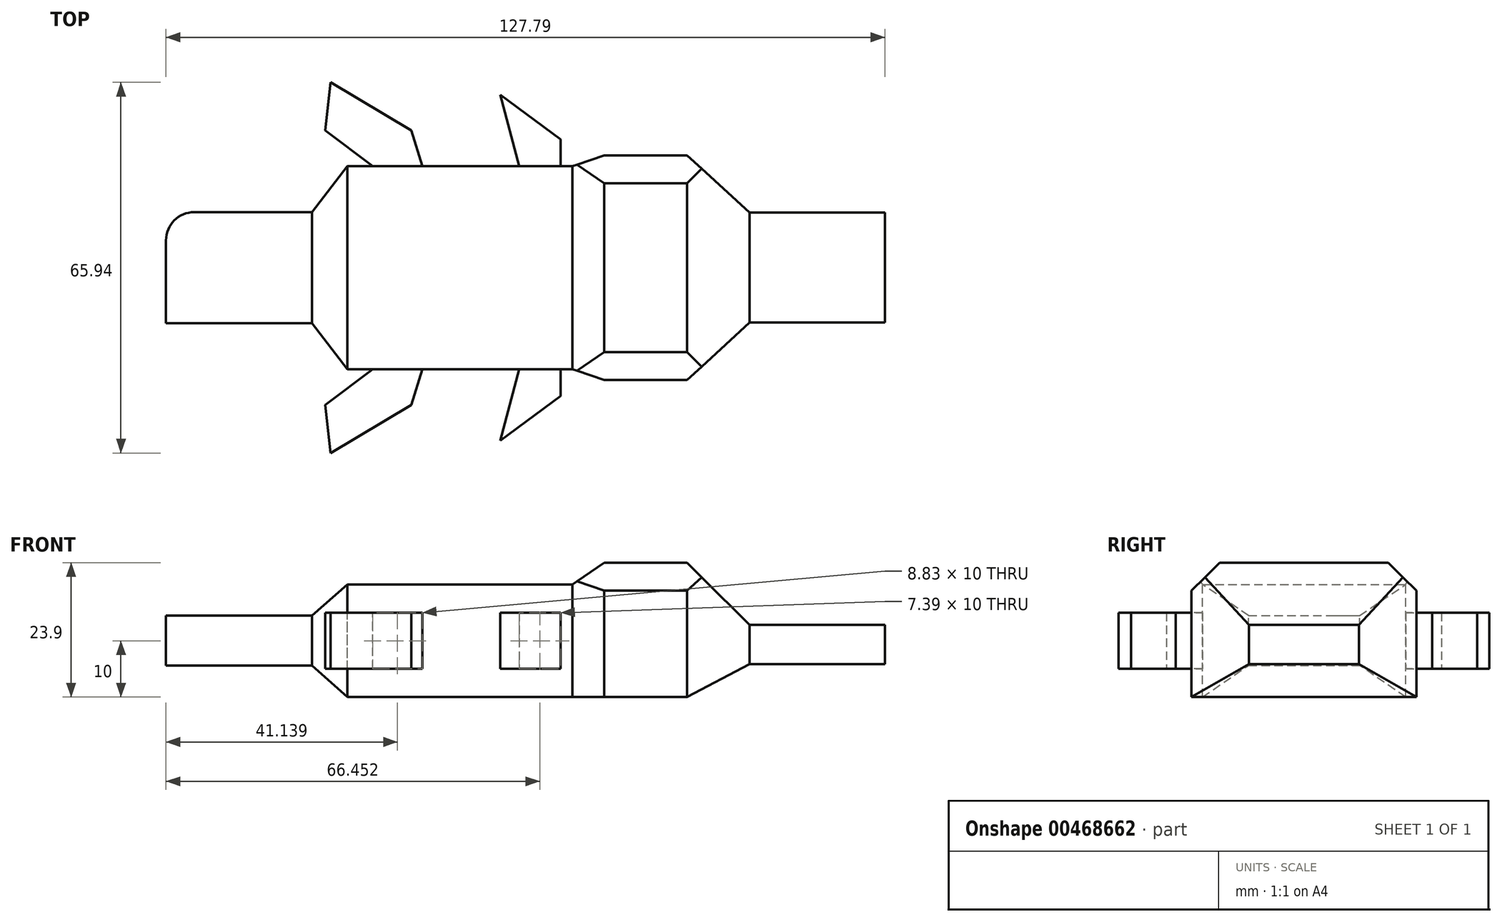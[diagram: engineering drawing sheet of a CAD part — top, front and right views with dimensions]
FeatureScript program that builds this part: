
annotation { "Feature Type Name" : "Feature", "Feature Type Description" : "" }
export const myFeature = defineFeature(function(context is Context, id is Id, definition is map)
    precondition{}
    {
        {
            var Q0;
            Q0=qCreatedBy(makeId("Front.planeOp"),FACE);
            var sketch = newSketch(context, id + "F0", { "sketchPlane" : qUnion([Q0])});
            skLineSegment(sketch, "E0.bottom", {"start": v(-20, 10) * mm, "end": v(20, 10) * mm});
            skLineSegment(sketch, "E0.top", {"start": v(-20, -10) * mm, "end": v(20, -10) * mm});
            skPoint(sketch, "E0.middle", {"position": v(0, 0) * mm});
            skLineSegment(sketch, "E1", {"start": v(20, 10) * mm, "end": v(25.66, 13.9) * mm});
            skLineSegment(sketch, "E2", {"start": v(25.66, 13.9) * mm, "end": v(40.35, 13.9) * mm});
            skLineSegment(sketch, "E3", {"start": v(20, -10) * mm, "end": v(40.35, -10) * mm});
            skLineSegment(sketch, "E4", {"start": v(-20, 10) * mm, "end": v(-26.29, 4.5) * mm});
            skLineSegment(sketch, "E5", {"start": v(-26.29, 4.5) * mm, "end": v(-52.26, 4.5) * mm});
            skLineSegment(sketch, "E6", {"start": v(-52.26, 4.5) * mm, "end": v(-52.26, -4.38) * mm});
            skLineSegment(sketch, "E7", {"start": v(-52.26, -4.38) * mm, "end": v(-26.29, -4.38) * mm});
            skLineSegment(sketch, "E8", {"start": v(-26.29, -4.38) * mm, "end": v(-20, -10) * mm});
            skPoint(sketch, "E9.endSnap0", {"position": v(45.99, 2.8) * mm});
            skLineSegment(sketch, "E10", {"start": v(51.46, 2.8) * mm, "end": v(75.53, 2.8) * mm});
            skLineSegment(sketch, "E11", {"start": v(51.46, -4.17) * mm, "end": v(75.53, -4.17) * mm});
            skLineSegment(sketch, "E12", {"start": v(75.53, 2.8) * mm, "end": v(75.53, -4.17) * mm});
            skPoint(sketch, "E13.orphan", {"position": v(75.53, -10) * mm});
            skPoint(sketch, "E14.orphan", {"position": v(63.42, -10) * mm});
            skPoint(sketch, "E15.end.orphan", {"position": v(44.28, 10) * mm});
            skLineSegment(sketch, "E16", {"start": v(51.46, 2.8) * mm, "end": v(40.35, 13.9) * mm});
            skLineSegment(sketch, "E17", {"start": v(51.46, -4.17) * mm, "end": v(40.35, -10) * mm});
            skSolve(sketch);
        }
        {
            var Q0;
            Q0=makeQuery(id+"F0.imprint","IMPRINT",FACE,{"disambiguationData":[TD([[makeQuery(id+"F0.imprint","IMPRINT",EDGE,{"derivedFrom":sQuery(id+"F0.wireOp",EDGE,"E0.bottom")}),-1.0]])]});
            var Q1;
            Q1=makeQuery(id+"F0.imprint","IMPRINT",FACE,{"disambiguationData":[TD([[makeQuery(id+"F0.imprint","IMPRINT",EDGE,{"derivedFrom":sQuery(id+"F0.wireOp",EDGE,"E0.left")}),-1.0]])]});
            var Q2;
            Q2=makeQuery(id+"F0.imprint","IMPRINT",FACE,{"disambiguationData":[TD([[makeQuery(id+"F0.imprint","IMPRINT",EDGE,{"derivedFrom":sQuery(id+"F0.wireOp",EDGE,"E0.right")}),1.0]])]});
            var Q3;
            {var subQ0=sQuery(id+"F0.wireOp",EDGE,"E9");Q3=makeQuery(id+"F0.imprint","IMPRINT",FACE,{"disambiguationData":[TD([[makeQuery(id+"F0.imprint","IMPRINT",EDGE,{"derivedFrom":subQ0}),-1.0]])]});}
            extrude(context, id + "F1", {"entities" : qUnion([Q0, Q1, Q2, Q3]), "endBound" : BoundingType.SYMMETRIC, "depth" : 40 * mm});
        }
        {
            var Q0;
            Q0=makeQuery(id+"F1.opExtrude","SWEPT_FACE",FACE,{"disambiguationData":[OSD([sQuery(id+"F0.wireOp",EDGE,"E0.bottom")])]});
            var sketch = newSketch(context, id + "F2", { "sketchPlane" : qUnion([Q0])});
            skLineSegment(sketch, "E18.MirrorCS", {"start": v(20, 18.06) * mm, "end": v(25.66, 20) * mm});
            skLineSegment(sketch, "E19.MirrorCS", {"start": v(-26.29, 9.87) * mm, "end": v(-73.86, 9.87) * mm});
            skLineSegment(sketch, "E20.MirrorCS", {"start": v(-20, 18.06) * mm, "end": v(20, 18.06) * mm});
            skLineSegment(sketch, "E21.MirrorCS", {"start": v(-20, 18.06) * mm, "end": v(-26.29, 9.87) * mm});
            skLineSegment(sketch, "E22", {"start": v(25.66, 20) * mm, "end": v(25.66, 20) * mm});
            skLineSegment(sketch, "E23", {"start": v(40.35, 20) * mm, "end": v(51.46, 9.78) * mm});
            skLineSegment(sketch, "E24", {"start": v(51.46, 9.78) * mm, "end": v(82.43, 9.78) * mm});
            skLineSegment(sketch, "E25.MirrorCS", {"start": v(20, -18.06) * mm, "end": v(25.66, -20) * mm});
            skLineSegment(sketch, "E26.MirrorCS", {"start": v(-20, -18.06) * mm, "end": v(-26.29, -9.87) * mm});
            skLineSegment(sketch, "E27.MirrorCS", {"start": v(-20, -18.06) * mm, "end": v(20, -18.06) * mm});
            skLineSegment(sketch, "E28.MirrorCS", {"start": v(-26.29, -9.87) * mm, "end": v(-73.86, -9.87) * mm});
            skLineSegment(sketch, "E29.MirrorCS", {"start": v(51.46, -9.78) * mm, "end": v(82.43, -9.78) * mm});
            skLineSegment(sketch, "E30.MirrorCS", {"start": v(25.66, -20) * mm, "end": v(25.66, -20) * mm});
            skLineSegment(sketch, "E31.MirrorCS", {"start": v(40.35, -20) * mm, "end": v(51.46, -9.78) * mm});
            skLineSegment(sketch, "E32", {"start": v(25.66, 20) * mm, "end": v(40.35, 20) * mm});
            skLineSegment(sketch, "E33", {"start": v(25.66, -20) * mm, "end": v(40.35, -20) * mm});
            skLineSegment(sketch, "E34", {"start": v(82.43, 9.78) * mm, "end": v(82.43, -9.78) * mm});
            skLineSegment(sketch, "E35", {"start": v(-73.86, -9.87) * mm, "end": v(-73.86, -40.04) * mm});
            skLineSegment(sketch, "E36", {"start": v(-73.86, -40.04) * mm, "end": v(108.4, -42.3) * mm});
            skLineSegment(sketch, "E37", {"start": v(108.4, -42.3) * mm, "end": v(105.7, 36.31) * mm});
            skLineSegment(sketch, "E38", {"start": v(105.7, 36.31) * mm, "end": v(-67.56, 60.93) * mm});
            skLineSegment(sketch, "E39", {"start": v(-67.56, 60.93) * mm, "end": v(-73.86, 9.87) * mm});
            skSolve(sketch);
        }
        {
            var Q0;
            Q0 = qSketchRegion(id + "F2", true);
            extrude(context, id + "F3", {"entities" : qUnion([Q0]), "operationType" : NewBodyOperationType.REMOVE, "endBound" : BoundingType.SYMMETRIC, "oppositeDirection" : true, "depth" : 86.8 * mm});
        }
        {
            var Q0;
            Q0=qCreatedBy(makeId("Top.planeOp"),FACE);
            var sketch = newSketch(context, id + "F4", { "sketchPlane" : qUnion([Q0])});
            skLineSegment(sketch, "E40", {"start": v(17.89, -14.75) * mm, "end": v(17.89, -22.8) * mm});
            skLineSegment(sketch, "E41", {"start": v(17.89, -22.8) * mm, "end": v(7.15, -30.76) * mm});
            skLineSegment(sketch, "E42", {"start": v(7.15, -30.76) * mm, "end": v(11.47, -14.37) * mm});
            skLineSegment(sketch, "E43", {"start": v(11.47, -14.37) * mm, "end": v(17.89, -14.75) * mm});
            skLineSegment(sketch, "E44", {"start": v(-11.15, -14.75) * mm, "end": v(-24, -24.44) * mm});
            skLineSegment(sketch, "E45", {"start": v(-24, -24.44) * mm, "end": v(-23.04, -32.97) * mm});
            skLineSegment(sketch, "E46", {"start": v(-23.04, -32.97) * mm, "end": v(-8.66, -24.44) * mm});
            skLineSegment(sketch, "E47", {"start": v(-8.66, -24.44) * mm, "end": v(-5.69, -14.75) * mm});
            skLineSegment(sketch, "E48", {"start": v(-5.69, -14.75) * mm, "end": v(-11.15, -14.75) * mm});
            skLineSegment(sketch, "E49.MirrorCS", {"start": v(-23.04, 32.97) * mm, "end": v(-8.66, 24.44) * mm});
            skLineSegment(sketch, "E50.MirrorCS", {"start": v(-8.66, 24.44) * mm, "end": v(-5.69, 14.75) * mm});
            skLineSegment(sketch, "E51.MirrorCS", {"start": v(-5.69, 14.75) * mm, "end": v(-11.15, 14.75) * mm});
            skLineSegment(sketch, "E52.MirrorCS", {"start": v(-24, 24.44) * mm, "end": v(-23.04, 32.97) * mm});
            skLineSegment(sketch, "E53.MirrorCS", {"start": v(-11.15, 14.75) * mm, "end": v(-24, 24.44) * mm});
            skLineSegment(sketch, "E54.MirrorCS", {"start": v(11.47, 14.37) * mm, "end": v(17.89, 14.75) * mm});
            skLineSegment(sketch, "E55.MirrorCS", {"start": v(7.15, 30.76) * mm, "end": v(11.47, 14.37) * mm});
            skLineSegment(sketch, "E56.MirrorCS", {"start": v(17.89, 22.8) * mm, "end": v(7.15, 30.76) * mm});
            skLineSegment(sketch, "E57.MirrorCS", {"start": v(17.89, 14.75) * mm, "end": v(17.89, 22.8) * mm});
            skSolve(sketch);
        }
        {
            var Q0;
            Q0 = qSketchRegion(id + "F4", true);
            extrude(context, id + "F5", {"entities" : qUnion([Q0]), "operationType" : NewBodyOperationType.ADD, "endBound" : BoundingType.SYMMETRIC, "depth" : 10 * mm});
        }
        {
            var Q0;
            Q0=makeQuery(id+"F3.boolean.opBoolean","INTERSECT",EDGE,{"derivedFrom":[makeQuery(id+"F1.opExtrude","SWEPT_FACE",FACE,{"disambiguationData":[OSD([sQuery(id+"F0.wireOp",EDGE,"E12")])]}),makeQuery(id+"F3.opExtrude","SWEPT_FACE",FACE,{"disambiguationData":[OSD([sQuery(id+"F2.wireOp",EDGE,"6TB88q83-F0ki-iJG8-r7gv-vxmnKUQgUbcT")])]})]});
            var Q1;
            Q1=makeQuery(id+"F3.boolean.opBoolean","INTERSECT",EDGE,{"derivedFrom":[makeQuery(id+"F1.opExtrude","SWEPT_FACE",FACE,{"disambiguationData":[OSD([sQuery(id+"F0.wireOp",EDGE,"E12")])]}),makeQuery(id+"F3.opExtrude","SWEPT_FACE",FACE,{"disambiguationData":[OSD([sQuery(id+"F2.wireOp",EDGE,"d585c033-5304-4f51-92d4-7f29337495183.MirrorCS")])]})]});
            var Q2;
            Q2=makeQuery(id+"F3.boolean.opBoolean","INTERSECT",EDGE,{"derivedFrom":[makeQuery(id+"F1.opExtrude","SWEPT_FACE",FACE,{"disambiguationData":[OSD([sQuery(id+"F0.wireOp",EDGE,"E6")])]}),makeQuery(id+"F3.opExtrude","SWEPT_FACE",FACE,{"disambiguationData":[OSD([sQuery(id+"F2.wireOp",EDGE,"UFveGuYq-JpYT-xMPh-vdc7-SJ4sFOseDCeF")])]})]});
            var Q3;
            Q3=makeQuery(id+"F3.boolean.opBoolean","INTERSECT",EDGE,{"derivedFrom":[makeQuery(id+"F1.opExtrude","SWEPT_FACE",FACE,{"disambiguationData":[OSD([sQuery(id+"F0.wireOp",EDGE,"E6")])]}),makeQuery(id+"F3.opExtrude","SWEPT_FACE",FACE,{"disambiguationData":[OSD([sQuery(id+"F2.wireOp",EDGE,"E19.MirrorCS")])]})]});
            fillet(context, id + "F6", {"entities" : qUnion([Q0, Q1, Q2, Q3]), "radius" : 5 * mm, "tangentPropagation" : true, "allowEdgeOverflow" : false});
        }
        {
            var Q0;
            Q0=makeQuery(id+"F1.opExtrude","SWEPT_FACE",FACE,{"disambiguationData":[OSD([sQuery(id+"F0.wireOp",EDGE,"E16")])]});
            var sketch = newSketch(context, id + "F7", { "sketchPlane" : qUnion([Q0])});
            skPoint(sketch, "E58.endSnap0", {"position": v(34.42, 0) * mm});
            skArc(sketch, "E59", {"start": v(22.68, -4.68) * mm, "mid": v(20.68, -6.68) * mm, "end": v(22.68, -8.68) * mm});
            skArc(sketch, "E60", {"start": v(26.24, -8.68) * mm, "mid": v(28.24, -6.68) * mm, "end": v(26.24, -4.68) * mm});
            skLineSegment(sketch, "E61", {"start": v(22.68, -8.68) * mm, "end": v(26.24, -8.68) * mm});
            skLineSegment(sketch, "E62", {"start": v(22.68, -4.68) * mm, "end": v(26.24, -4.68) * mm});
            skCircle(sketch, "E63", {"center": v(26.24, -6.68) * mm, "radius": 1.49 * mm});
            skCircle(sketch, "E64.MirrorC", {"center": v(26.24, 6.68) * mm, "radius": 1.49 * mm});
            skArc(sketch, "E65.MirrorCS", {"start": v(26.24, 8.68) * mm, "mid": v(28.24, 6.68) * mm, "end": v(26.24, 4.68) * mm});
            skArc(sketch, "E66.MirrorCS", {"start": v(22.68, 4.68) * mm, "mid": v(20.68, 6.68) * mm, "end": v(22.68, 8.68) * mm});
            skLineSegment(sketch, "E67.MirrorCS", {"start": v(22.68, 8.68) * mm, "end": v(26.24, 8.68) * mm});
            skLineSegment(sketch, "E68.MirrorCS", {"start": v(22.68, 4.68) * mm, "end": v(26.24, 4.68) * mm});
            skSolve(sketch);
        }
        {
            var Q0;
            Q0=makeQuery(id+"F1.opExtrude","CAP_EDGE",EDGE,{"disambiguationData":[OSD([sQuery(id+"F0.wireOp",EDGE,"E2")])],"isStart":false});
            var Q1;
            Q1=makeQuery(id+"F1.opExtrude","CAP_EDGE",EDGE,{"disambiguationData":[OSD([sQuery(id+"F0.wireOp",EDGE,"E2")])],"isStart":true});
            chamfer(context, id + "F8", {"entities" : qUnion([Q0, Q1]), "width" : 5 * mm, "tangentPropagation" : true});
        }
    });
